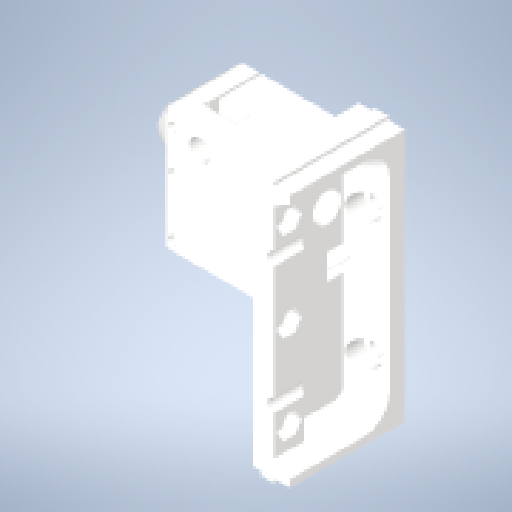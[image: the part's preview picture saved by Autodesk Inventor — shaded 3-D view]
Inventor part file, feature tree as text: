
AUTODESK INVENTOR PART (.ipt)
format: ipt  version: 2024 (Build 280153000, 153)  size: 2,249,216 bytes
history: native  units: mm
features: sketch x39, fillet x31, projected_geometry x28, extrude x27, hole x17, plane x11, other x10, chamfer x7, surface_op x3, thicken_offset x2, mirror x1, revolve x1, split x1
ambient origin geometry x8: Origin, YZ Plane, XZ Plane, XY Plane, X Axis, Y Axis, Z Axis, Center Point
bodies: Solid1 (feature_tree)
feature tree (178):
  extrude  "Extrusion1"  Depth=99.75mm
  extrude  "Extrusion2"  Depth=48.0mm
  plane  "Work Plane2"
  extrude  "Extrusion6"  Depth=50.0mm TaperAngle=0.0deg
  extrude  "Extrusion7"  Depth=12.1mm
  extrude  "Extrusion8"  Depth=51.0mm
  extrude  "Extrusion9"  Depth=16.4mm
  sketch  "Sketch11"  dims[d34=2.37mm d35=0.0mm d36=8.8mm]
  hole  "Hole2"  [1 undecoded]
  hole  "Hole3"  [1 undecoded]
  plane  "Work Plane3"
  plane  "Work Plane5"
  sketch  "Sketch13"  dims[d37=14.8mm d38=0.0mm d39=7.25mm]
  extrude  "Extrusion10"  TaperAngle=180.0deg  [1 undecoded]
  extrude  "Extrusion11"  Depth=4.3mm
  extrude  "Extrusion12"  Depth=7.6mm
  hole  "Hole4"  [1 undecoded]
  extrude  "Extrusion13"  Depth=3.0mm
  plane  "Work Plane6"
  extrude  "Extrusion14"  Depth=12.56mm
  extrude  "Extrusion15"  Depth=5.08mm
  hole  "Hole5"  [1 undecoded]
  extrude  "Extrusion19"  Depth=8.8mm
  extrude  "Extrusion20"  Depth=9.5mm
  extrude  "Extrusion21"  Depth=5.0mm
  extrude  "Extrusion22"  Depth=1.5mm
  fillet  "Fillet3"  Radius=1.5mm
  chamfer  "Chamfer2"  Distance=36.0mm
  hole  "Hole6"  [1 undecoded]
  extrude  "Extrusion23"  Depth=3.0mm
  chamfer  "Chamfer3"  [1 undecoded]
  extrude  "Extrusion24"  Depth=10.0mm
  hole  "Hole7"  [1 undecoded]
  plane  "Work Plane7"
  hole  "Hole8"  [1 undecoded]
  extrude  "Extrusion25"  Depth=5.0mm TaperAngle=30.0deg
  hole  "Hole9"  [1 undecoded]
  chamfer  "Chamfer4"  Distance=12.0mm
  plane  "Work Plane8"
  fillet  "Fillet4"  Radius=6.0mm
  hole  "Hole11"  [1 undecoded]
  hole  "Hole12"  [1 undecoded]
  hole  "Hole13"  [1 undecoded]
  hole  "Hole14"  [1 undecoded]
  hole  "Hole15"  [1 undecoded]
  extrude  "Extrusion26"  Depth=1.0mm
  chamfer  "Chamfer5"  Distance=0.75mm Angle=15.0deg
  chamfer  "Chamfer6"  Distance=0.75mm Angle=15.0deg
  fillet  "Fillet6"  Radius=3.0mm
  chamfer  "Chamfer7"  Distance=2.0mm Angle=15.0deg
  fillet  "Fillet7"  Radius=0.5mm
  fillet  "Fillet9"  Radius=1.0mm
  fillet  "Fillet10"  Radius=1.0mm
  fillet  "Fillet11"  Radius=0.5mm
  fillet  "Fillet14"  Radius=2.0mm
  fillet  "Fillet15"  Radius=0.5mm
  thicken_offset  "Thicken1"
  fillet  "Fillet16"  Radius=15.7mm
  hole  "Hole16"  [1 undecoded]
  sketch  "Sketch44"  dims[d151=5.0mm d152=0.0mm d153=5.0mm d154=2.0mm d155=30.0deg]
  extrude  "Extrusion30"  Depth=0.5mm
  extrude  "Extrusion31"  TaperAngle=150.0deg  [1 undecoded]
  fillet  "Fillet17"  Radius=10.0mm
  plane  "Work Plane9"
  hole  "Hole17"  [1 undecoded]
  plane  "Work Plane10"
  mirror  "Mirror1"
  fillet  "Fillet18"  Radius=6.0mm
  fillet  "Fillet19"  Radius=0.25mm
  fillet  "Fillet20"  Radius=2.0mm
  fillet  "Fillet21"  Radius=0.25mm
  fillet  "Fillet22"  Radius=0.5mm
  fillet  "Fillet23"  Radius=10.0mm
  fillet  "Fillet24"  Radius=0.5mm
  fillet  "Fillet25"  Radius=0.5mm
  hole  "Hole18"  [1 undecoded]
  fillet  "Fillet26"  Radius=0.25mm
  fillet  "Fillet27"  Radius=3.5mm
  fillet  "Fillet28"  Radius=3.5mm
  plane  "Work Plane11"
  revolve  "Revolution1"  [1 undecoded]
  extrude  "Extrusion32"  Depth=0.5mm
  chamfer  "Chamfer8"  Distance=5.7mm
  fillet  "Fillet29"  Radius=8.0mm
  fillet  "Fillet30"  Radius=6.0mm
  fillet  "Fillet32"  Radius=0.5mm
  hole  "Hole19"  [1 undecoded]
  fillet  "Fillet33"  Radius=0.5mm
  plane  "Work Plane12"
  sketch  "Sketch54"  dims[d176=5.2mm]
  surface_op  "Trim1"
  fillet  "Fillet36"  Radius=1.0mm
  surface_op  "Stitch Surface1"
  fillet  "Fillet34"  Radius=0.5mm
  split  "Split2"
  thicken_offset  "Thicken3"
  fillet  "Fillet35"  Radius=1.0mm
  extrude  "Extrusion34"  Depth=0.5mm TaperAngle=0.0deg
  fillet  "Fillet37"  Radius=0.5mm
  fillet  "Fillet38"  Radius=0.5mm
  sketch  "Sketch1"  dims[d0=18.0mm d1=99.75mm]
  sketch  "Sketch2"  dims[d2=45.0mm d3=0.0mm d4=48.0mm]
  sketch  "Sketch7"  dims[d5=50.0mm d6=30.0mm d7=0.0mm]
  sketch  "Sketch8"  dims[d27=-7.5mm d28=12.1mm]
  sketch  "Sketch9"  dims[d29=18.0mm d30=51.0mm]
  sketch  "Sketch10"  dims[d31=5.0mm d32=0.0mm d33=16.4mm]
  other  "Work Axis1"
  plane  "Work Plane4"
  sketch  "Sketch15"  dims[d40=0.2mm d41=0.0mm]
  sketch  "Sketch16"  dims[d42=3.2mm d43=6.0mm d44=4.0mm d45=2.0mm d46=90.0deg d47=4.7mm d48=0.0mm]
  sketch  "Sketch17"  dims[d49=3.2mm d50=6.0mm d51=4.0mm d52=2.0mm d53=90.0deg d54=16.3mm d55=0.0mm d59=180.0deg d60=-11.0mm]
  sketch  "Sketch21"  dims[d61=5.1mm d62=4.3mm]
  sketch  "Sketch22"  dims[d63=5.7mm d64=0.0mm d65=7.6mm]
  projected_geometry  "Projected Loop6"
  sketch  "Sketch23"  dims[d66=8.5mm d67=1.5mm d68=0.0mm]
  projected_geometry  "Projected Loop7"
  sketch  "Sketch24"  dims[d69=11.2mm d70=3.0mm]
  projected_geometry  "Projected Loop8"
  sketch  "Sketch25"  dims[d72=19.0mm d73=0.0mm d74=12.56mm]
  projected_geometry  "Projected Loop9"
  sketch  "Sketch26"  dims[d75=1.75mm d76=6.0mm d77=4.0mm d78=2.0mm d79=90.0deg d80=9.0mm d81=20.594885mm d82=5.08mm]
  projected_geometry  "Projected Loop10"
  sketch  "Sketch27"  dims[d83=2.0mm d84=13.75mm]
  projected_geometry  "Projected Loop11"
  sketch  "Sketch28"  dims[d85=2.5mm d86=0.0mm d88=8.8mm]
  projected_geometry  "Projected Loop12"
  sketch  "Sketch29"  dims[d89=13.0mm d90=9.5mm]
  sketch  "Sketch30"  dims[d91=5.25mm d92=0.0mm d93=5.0mm]
  sketch  "Sketch31"  dims[d94=0.5mm d95=0.0mm]
  sketch  "Sketch33"  dims[d96=3.3mm d97=6.0mm d98=4.0mm d99=2.0mm d100=90.0deg d101=9.0mm d102=20.594885mm d123=5.5mm d124=1.5mm d125=36.0mm d126=0.0mm]
  projected_geometry  "Projected Loop13"
  sketch  "Sketch34"  dims[d127=12.25mm d128=3.5mm d129=0.0mm]
  sketch  "Sketch35"  dims[d130=3.0mm d131=3.0mm]
  sketch  "Sketch36"  dims[d132=3.0mm d133=0.0mm d134=0.0mm]
  sketch  "Sketch37"  dims[d135=6.0mm d136=0.0mm d137=10.0mm]
  sketch  "Sketch38"  dims[d138=11.5mm d139=2.0mm d140=30.0deg d141=70.0mm]
  sketch  "Sketch39"  dims[d142=6.0mm]
  projected_geometry  "Projected Loop14"
  projected_geometry  "Projected Loop15"
  other  "Srf1"
  sketch  "Sketch43"  dims[d143=5.3mm d144=6.0mm d145=4.0mm d146=2.0mm d147=90.0deg d148=8.0mm d149=20.594885mm d150=12.0mm]
  projected_geometry  "Projected Loop32"
  projected_geometry  "Projected Loop33"
  projected_geometry  "Projected Loop34"
  projected_geometry  "Projected Loop35"
  projected_geometry  "Projected Loop36"
  sketch  "Sketch45"  dims[d156=8.25mm d157=5.0mm d158=0.0mm]
  sketch  "Sketch46"  dims[d159=50.0mm]
  other  "Srf2"
  sketch  "Sketch47"  dims[d160=5.3mm d161=6.0mm d162=4.0mm d163=2.0mm d164=90.0deg d165=8.0mm d166=20.594885mm]
  other  "Work Axis2"
  other  "Work Axis3"
  sketch  "Sketch48"  dims[d167=-5.0mm]
  projected_geometry  "Projected Loop37"
  sketch  "Sketch49"  dims[d168=10.0mm d169=6.0mm d170=4.0mm d171=2.0mm d172=90.0deg d173=8.0mm d174=20.594885mm]
  projected_geometry  "Projected Loop38"
  sketch  "Sketch52"  dims[d175=2.2mm]
  other  "Srf5"
  other  "Srf6"
  other  "Srf7"
  sketch  "Sketch55"  dims[d177=8.6mm d178=12.0mm d179=6.0mm d180=0.0mm d181=8.35mm d182=6.0mm d183=4.0mm d184=2.0mm d185=90.0deg d186=7.3mm d187=0.0mm d188=6.0mm d189=2.0mm d190=30.0deg d198=4.0mm d199=11.5mm d200=6.0mm d201=4.0mm d202=2.0mm d203=90.0deg d204=8.0mm d205=0.0mm d206=8.35mm d207=6.0mm d208=4.0mm d209=2.0mm d210=90.0deg d211=7.3mm d212=0.0mm d213=4.4mm d214=6.0mm d215=4.0mm d216=2.0mm d217=90.0deg d218=6.0mm d219=0.0mm d220=4.4mm d221=6.0mm d222=4.0mm d223=2.0mm d224=90.0deg d225=15.0mm d226=0.0mm d227=2.0mm d228=6.0mm d229=4.0mm d230=2.0mm d231=90.0deg d232=15.0mm d233=0.0mm d234=10.0mm d235=30.0deg d236=30.0mm d237=0.0mm d238=1.0mm d239=0.75mm d240=2.0mm d241=15.0deg d242=0.75mm d243=2.0mm d244=15.0deg d246=3.0mm d247=2.0mm d248=2.0mm d249=15.0deg d250=0.5mm d252=1.0mm d253=1.0mm d254=0.5mm d257=2.0mm d258=0.5mm d260=15.7mm d261=3.0mm d262=2.0mm d263=150.0deg d264=10.0mm d265=20.0mm d266=6.0mm d267=0.25mm d268=2.0mm d269=0.25mm d270=0.5mm d271=10.0mm d272=0.0mm d273=0.5mm d274=0.5mm d287=19.0mm d288=0.25mm d289=3.5mm d290=3.5mm d291=16.0mm d292=5.7mm d293=5.7mm d294=3.3mm d295=6.0mm d296=4.0mm d297=2.0mm d298=90.0deg d299=6.0mm d300=0.0mm d301=5.7mm d302=8.0mm d303=0.0mm d304=6.0mm d305=0.0mm d306=0.5mm d307=-2.25mm d308=8.75mm d309=6.0mm d310=4.0mm d311=2.0mm d312=90.0deg d313=1.0mm d314=0.0mm d315=0.5mm d316=1.0mm d317=0.5mm d318=1.0mm d319=6.0mm d320=0.0mm d321=0.5mm d322=0.5mm d323=0.5mm d324=0.5mm d325=0.5mm d326=0.5mm d327=5.0mm d328=6.0mm d329=4.0mm d330=2.0mm d331=90.0deg d332=1.0mm d333=0.0mm d334=1.0mm d335=0.5mm d336=0.5mm d338=0.0mm d339=8.2mm d340=45.0deg d341=10.75mm d342=22.5deg d343=45.0deg d344=1.75mm d345=0.0mm d346=1.175mm d347=1.175mm d348=2.0mm d349=45.0deg d350=0.5mm d351=0.5mm d353=0.5mm d361=8.0mm d362=6.0mm d363=4.0mm d364=2.0mm d365=90.0deg d366=8.0mm d367=0.0mm d368=0.5mm d373=0.0mm d374=0.2mm d375=0.2mm d376=0.2mm d377=6.0mm d378=1.0mm d380=0.4mm d381=0.0mm d382=5.0mm d383=0.0mm d384=0.2mm d385=0.4mm d386=1.0mm d387=0.5mm d388=0.5mm d389=0.0mm d390=0.5mm d391=0.5mm d111=0.5mm d112=0.872665mm d113=0.5mm d114=0.872665mm d352=0.0mm d354=0.0mm d355=0.0mm d392=0.0mm d393=0.0mm]
  projected_geometry  "Projected Loop42"
  extrude  "ExtrusionSrf1"  Depth=0.5mm
  extrude  "ExtrusionSrf2"  Depth=0.5mm
  extrude  "ExtrusionSrf4"  Depth=0.5mm
  surface_op  "Boundary Patch1"
  projected_geometry  "Project Cut Edges2"
  projected_geometry  "Project Cut Edges3"
  projected_geometry  "Project Cut Edges4"
  projected_geometry  "Project Cut Edges5"
  projected_geometry  "Project Cut Edges6"
  projected_geometry  "Project Cut Edges7"
  projected_geometry  "Project Cut Edges8"
  projected_geometry  "Project Cut Edges11"
  projected_geometry  "Project Cut Edges12"
  projected_geometry  "Project Cut Edges13"
  other  "Filament Motion Sensor Base"
  other  "Filmament Motion Sensor Cap"
note: 21 required parameter values undecoded (feature->parameter linkage not recoverable at this tier; creation-order binding heuristic only, values carry confidence <= 0.55)